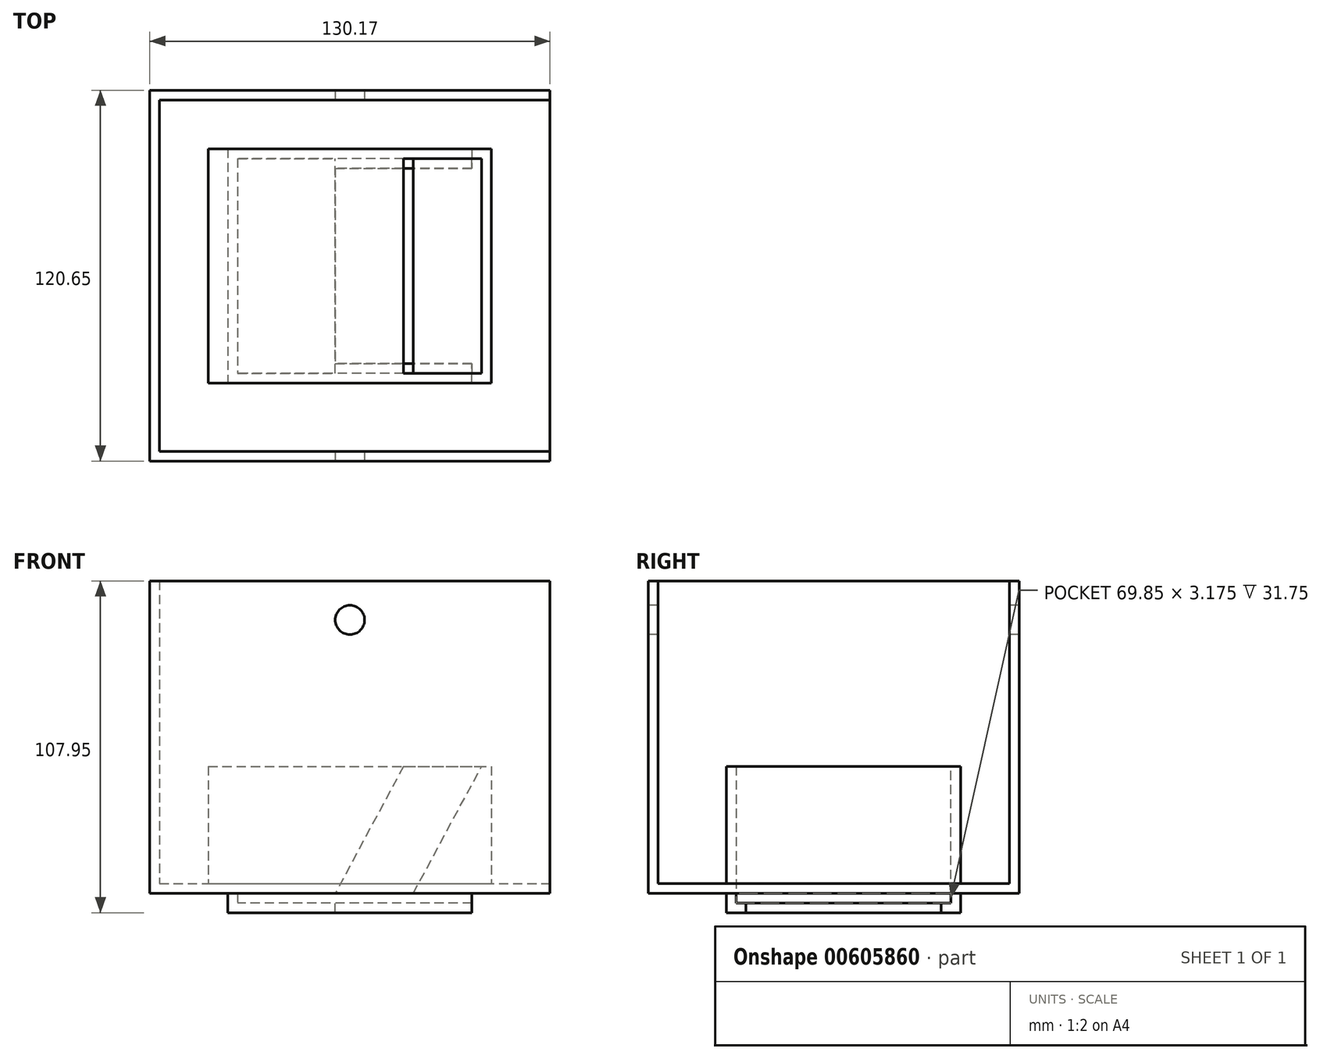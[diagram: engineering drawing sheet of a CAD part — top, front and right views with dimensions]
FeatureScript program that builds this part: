
annotation { "Feature Type Name" : "Feature", "Feature Type Description" : "" }
export const myFeature = defineFeature(function(context is Context, id is Id, definition is map)
    precondition{}
    {
        {
            var Q0;
            Q0=qCreatedBy(makeId("Top.planeOp"),FACE);
            var sketch = newSketch(context, id + "F0", { "sketchPlane" : qUnion([Q0])});
            skLineSegment(sketch, "E0.bottom", {"start": v(179.28, 0) * mm, "end": v(309.45, 0) * mm});
            skLineSegment(sketch, "E0.top", {"start": v(179.28, 120.65) * mm, "end": v(309.45, 120.65) * mm});
            skLineSegment(sketch, "E0.left", {"start": v(179.28, 0) * mm, "end": v(179.28, 120.65) * mm});
            skLineSegment(sketch, "E0.right", {"start": v(309.45, 0) * mm, "end": v(309.45, 120.65) * mm});
            skSolve(sketch);
        }
        {
            var Q0;
            Q0=makeQuery(id+"F0.imprint","IMPRINT",FACE,{"disambiguationData":[TD([[makeQuery(id+"F0.imprint","IMPRINT",EDGE,{"derivedFrom":sQuery(id+"F0.wireOp",EDGE,"E0.bottom")}),1.0]])]});
            extrude(context, id + "F1", {"entities" : qUnion([Q0]), "depth" : 101.6 * mm, "offsetDistance" : 25.4 * mm});
        }
        {
            var Q0;
            Q0=makeQuery(id+"F1.opExtrude","CAP_FACE",FACE,{"disambiguationData":[OSD([sQuery(id+"F0.wireOp",EDGE,"E0.bottom"),sQuery(id+"F0.wireOp",EDGE,"E0.top"),sQuery(id+"F0.wireOp",EDGE,"E0.left"),sQuery(id+"F0.wireOp",EDGE,"E0.right")])],"isStart":false});
            shell(context, id + "F2", {"entities" : qUnion([Q0]), "thickness" : 3.17 * mm});
        }
        {
            var Q0;
            Q0=makeQuery(id+"F2.opShell","OFFSET_FACE",FACE,{"disambiguationData":[OSD([sQuery(id+"F0.wireOp",EDGE,"E0.bottom"),sQuery(id+"F0.wireOp",EDGE,"E0.top"),sQuery(id+"F0.wireOp",EDGE,"E0.left"),sQuery(id+"F0.wireOp",EDGE,"E0.right")])]});
            var sketch = newSketch(context, id + "F3", { "sketchPlane" : qUnion([Q0])});
            skLineSegment(sketch, "E1.bottom", {"start": v(201.5, 98.43) * mm, "end": v(287.23, 98.43) * mm});
            skLineSegment(sketch, "E1.top", {"start": v(201.5, 28.58) * mm, "end": v(287.23, 28.58) * mm});
            skLineSegment(sketch, "E1.left", {"start": v(201.5, 98.43) * mm, "end": v(201.5, 28.58) * mm});
            skLineSegment(sketch, "E1.right", {"start": v(287.23, 98.43) * mm, "end": v(287.23, 28.58) * mm});
            skSolve(sketch);
        }
        {
            var Q0;
            Q0=makeQuery(id+"F3.imprint","IMPRINT",FACE,{"disambiguationData":[TD([[makeQuery(id+"F3.imprint","IMPRINT",EDGE,{"derivedFrom":sQuery(id+"F3.wireOp",EDGE,"E1.bottom")}),-1.0]])]});
            extrude(context, id + "F4", {"entities" : qUnion([Q0]), "operationType" : NewBodyOperationType.REMOVE, "oppositeDirection" : true, "depth" : 25.4 * mm, "offsetDistance" : 25.4 * mm});
        }
        {
            var Q0;
            Q0=makeQuery(id+"F2.opShell","OFFSET_FACE",FACE,{"disambiguationData":[OSD([sQuery(id+"F0.wireOp",EDGE,"E0.bottom"),sQuery(id+"F0.wireOp",EDGE,"E0.top"),sQuery(id+"F0.wireOp",EDGE,"E0.left"),sQuery(id+"F0.wireOp",EDGE,"E0.right")])]});
            var sketch = newSketch(context, id + "F5", { "sketchPlane" : qUnion([Q0])});
            skLineSegment(sketch, "E2.top", {"start": v(198.33, 25.4) * mm, "end": v(290.4, 25.4) * mm});
            skLineSegment(sketch, "E2.left", {"start": v(198.33, 101.6) * mm, "end": v(198.33, 25.4) * mm});
            skLineSegment(sketch, "E2.right", {"start": v(290.4, 101.6) * mm, "end": v(290.4, 25.4) * mm});
            skLineSegment(sketch, "E3", {"start": v(198.33, 101.6) * mm, "end": v(290.4, 101.6) * mm});
            skSolve(sketch);
        }
        {
            var Q0;
            Q0=makeQuery(id+"F5.imprint","IMPRINT",FACE,{"disambiguationData":[TD([[makeQuery(id+"F5.imprint","IMPRINT",EDGE,{"derivedFrom":sQuery(id+"F5.wireOp",EDGE,"E2.top")}),1.0]])]});
            extrude(context, id + "F6", {"entities" : qUnion([Q0]), "operationType" : NewBodyOperationType.ADD, "depth" : 38.1 * mm, "offsetDistance" : 25.4 * mm});
        }
        {
            var Q0;
            Q0=makeQuery(id+"F1.opExtrude","CAP_FACE",FACE,{"disambiguationData":[OSD([sQuery(id+"F0.wireOp",EDGE,"E0.bottom"),sQuery(id+"F0.wireOp",EDGE,"E0.top"),sQuery(id+"F0.wireOp",EDGE,"E0.left"),sQuery(id+"F0.wireOp",EDGE,"E0.right")])],"isStart":true});
            var sketch = newSketch(context, id + "F7", { "sketchPlane" : qUnion([Q0])});
            skLineSegment(sketch, "E4", {"start": v(204.68, -28.58) * mm, "end": v(204.68, -25.4) * mm});
            skLineSegment(sketch, "E5", {"start": v(204.68, -25.4) * mm, "end": v(284.05, -25.4) * mm});
            skLineSegment(sketch, "E6", {"start": v(284.05, -25.4) * mm, "end": v(284.05, -28.58) * mm});
            skSolve(sketch);
        }
        {
            var Q0;
            Q0 = qSketchRegion(id + "F7", true);
            var Q1;
            {var subQ0=sQuery(id+"F7.wireOp",EDGE,"E4");Q1=makeQuery(id+"F7.imprint","IMPRINT",FACE,{"disambiguationData":[TD([[makeQuery(id+"F7.imprint","IMPRINT",EDGE,{"derivedFrom":subQ0}),-1.0]])]});}
            extrude(context, id + "F8", {"entities" : qUnion([Q0, Q1]), "operationType" : NewBodyOperationType.ADD, "depth" : 6.35 * mm, "offsetDistance" : 25.4 * mm});
        }
        {
            var Q0;
            Q0=makeQuery(id+"F1.opExtrude","CAP_FACE",FACE,{"disambiguationData":[OSD([sQuery(id+"F0.wireOp",EDGE,"E0.bottom"),sQuery(id+"F0.wireOp",EDGE,"E0.top"),sQuery(id+"F0.wireOp",EDGE,"E0.left"),sQuery(id+"F0.wireOp",EDGE,"E0.right")])],"isStart":true});
            var sketch = newSketch(context, id + "F9", { "sketchPlane" : qUnion([Q0])});
            skLineSegment(sketch, "E7", {"start": v(204.68, -98.43) * mm, "end": v(204.68, -101.6) * mm});
            skLineSegment(sketch, "E8", {"start": v(204.68, -101.6) * mm, "end": v(284.05, -101.6) * mm});
            skLineSegment(sketch, "E9", {"start": v(284.05, -101.6) * mm, "end": v(284.05, -98.43) * mm});
            skSolve(sketch);
        }
        {
            var Q0;
            {var subQ0=sQuery(id+"F9.wireOp",EDGE,"E7");Q0=makeQuery(id+"F9.imprint","IMPRINT",FACE,{"disambiguationData":[TD([[makeQuery(id+"F9.imprint","IMPRINT",EDGE,{"derivedFrom":subQ0}),1.0]])]});}
            extrude(context, id + "F10", {"entities" : qUnion([Q0]), "operationType" : NewBodyOperationType.ADD, "depth" : 6.35 * mm, "offsetDistance" : 25.4 * mm});
        }
        {
            var Q0;
            {var subQ0=sQuery(id+"F3.wireOp",EDGE,"E1.bottom");Q0=makeQuery(id+"F10.boolean.opBoolean","MERGE",FACE,{"derivedFrom":[makeQuery(id+"F6.boolean.opBoolean","MERGE",FACE,{"derivedFrom":[makeQuery(id+"F4.boolean.opBoolean","COPY",FACE,{"derivedFrom":makeQuery(id+"F4.opExtrude","SWEPT_FACE",FACE,{"disambiguationData":[OSD([subQ0])]})}),makeQuery(id+"F6.opExtrude","SWEPT_FACE",FACE,{"disambiguationData":[OSD([subQ0])]})]}),makeQuery(id+"F10.opExtrude","SWEPT_FACE",FACE,{"disambiguationData":[OSD([sQuery(id+"F0.wireOp",EDGE,"E0.bottom"),sQuery(id+"F0.wireOp",EDGE,"E0.top"),sQuery(id+"F0.wireOp",EDGE,"E0.left"),sQuery(id+"F0.wireOp",EDGE,"E0.right"),subQ0])]})]});}
            var sketch = newSketch(context, id + "F11", { "sketchPlane" : qUnion([Q0])});
            skLineSegment(sketch, "E10.bottom", {"start": v(284.05, -6.35) * mm, "end": v(204.68, -6.35) * mm});
            skLineSegment(sketch, "E10.top", {"start": v(284.05, -3.18) * mm, "end": v(204.68, -3.18) * mm});
            skLineSegment(sketch, "E10.left", {"start": v(284.05, -6.35) * mm, "end": v(284.05, -3.18) * mm});
            skLineSegment(sketch, "E10.right", {"start": v(204.68, -6.35) * mm, "end": v(204.68, -3.18) * mm});
            skSolve(sketch);
        }
        {
            var Q0;
            Q0=makeQuery(id+"F11.imprint","IMPRINT",FACE,{"disambiguationData":[TD([[makeQuery(id+"F11.imprint","IMPRINT",EDGE,{"derivedFrom":sQuery(id+"F11.wireOp",EDGE,"E10.bottom")}),1.0]])]});
            extrude(context, id + "F12", {"entities" : qUnion([Q0]), "operationType" : NewBodyOperationType.ADD, "depth" : 3.17 * mm, "offsetDistance" : 25.4 * mm});
        }
        {
            var Q0;
            {var subQ0=sQuery(id+"F3.wireOp",EDGE,"E1.top");Q0=makeQuery(id+"F8.boolean.opBoolean","MERGE",FACE,{"derivedFrom":[makeQuery(id+"F6.boolean.opBoolean","MERGE",FACE,{"derivedFrom":[makeQuery(id+"F4.boolean.opBoolean","COPY",FACE,{"derivedFrom":makeQuery(id+"F4.opExtrude","SWEPT_FACE",FACE,{"disambiguationData":[OSD([subQ0])]})}),makeQuery(id+"F6.opExtrude","SWEPT_FACE",FACE,{"disambiguationData":[OSD([subQ0])]})]}),makeQuery(id+"F8.opExtrude","SWEPT_FACE",FACE,{"disambiguationData":[OSD([sQuery(id+"F0.wireOp",EDGE,"E0.bottom"),sQuery(id+"F0.wireOp",EDGE,"E0.top"),sQuery(id+"F0.wireOp",EDGE,"E0.left"),sQuery(id+"F0.wireOp",EDGE,"E0.right"),subQ0])]})]});}
            var sketch = newSketch(context, id + "F13", { "sketchPlane" : qUnion([Q0])});
            skLineSegment(sketch, "E11.bottom", {"start": v(-284.05, -6.35) * mm, "end": v(-204.68, -6.35) * mm});
            skLineSegment(sketch, "E11.top", {"start": v(-284.05, -3.18) * mm, "end": v(-204.68, -3.18) * mm});
            skLineSegment(sketch, "E11.left", {"start": v(-284.05, -6.35) * mm, "end": v(-284.05, -3.18) * mm});
            skLineSegment(sketch, "E11.right", {"start": v(-204.68, -6.35) * mm, "end": v(-204.68, -3.18) * mm});
            skSolve(sketch);
        }
        {
            var Q0;
            Q0=makeQuery(id+"F13.imprint","IMPRINT",FACE,{"disambiguationData":[TD([[makeQuery(id+"F13.imprint","IMPRINT",EDGE,{"derivedFrom":sQuery(id+"F13.wireOp",EDGE,"E11.bottom")}),-1.0]])]});
            extrude(context, id + "F14", {"entities" : qUnion([Q0]), "operationType" : NewBodyOperationType.ADD, "depth" : 3.17 * mm, "offsetDistance" : 25.4 * mm});
        }
        {
            var Q0;
            Q0=makeQuery(id+"F1.opExtrude","SWEPT_FACE",FACE,{"disambiguationData":[OSD([sQuery(id+"F0.wireOp",EDGE,"E0.right")])]});
            var sketch = newSketch(context, id + "F15", { "sketchPlane" : qUnion([Q0])});
            skLineSegment(sketch, "E12.bottom", {"start": v(3.17, 98.43) * mm, "end": v(117.47, 98.43) * mm});
            skLineSegment(sketch, "E12.top", {"start": v(3.17, 3.18) * mm, "end": v(117.47, 3.18) * mm});
            skLineSegment(sketch, "E12.left", {"start": v(3.17, 98.43) * mm, "end": v(3.17, 3.17) * mm});
            skLineSegment(sketch, "E12.right", {"start": v(117.47, 98.43) * mm, "end": v(117.47, 3.17) * mm});
            skSolve(sketch);
        }
        {
            var Q0;
            Q0=makeQuery(id+"F15.imprint","IMPRINT",FACE,{"disambiguationData":[TD([[makeQuery(id+"F15.imprint","IMPRINT",EDGE,{"derivedFrom":sQuery(id+"F15.wireOp",EDGE,"E12.bottom")}),-1.0]])]});
            extrude(context, id + "F16", {"entities" : qUnion([Q0]), "operationType" : NewBodyOperationType.REMOVE, "oppositeDirection" : true, "depth" : 6.35 * mm, "offsetDistance" : 25.4 * mm});
        }
        {
            var Q0;
            Q0=makeQuery(id+"F1.opExtrude","SWEPT_FACE",FACE,{"disambiguationData":[OSD([sQuery(id+"F0.wireOp",EDGE,"E0.right")])]});
            var sketch = newSketch(context, id + "F17", { "sketchPlane" : qUnion([Q0])});
            skLineSegment(sketch, "E13", {"start": v(3.17, 98.43) * mm, "end": v(3.17, 101.6) * mm});
            skLineSegment(sketch, "E14", {"start": v(117.47, 98.43) * mm, "end": v(117.47, 101.6) * mm});
            skSolve(sketch);
        }
        {
            var Q0;
            Q0 = qSketchRegion(id + "F17", true);
            var Q1;
            {var subQ0=sQuery(id+"F17.wireOp",EDGE,"E13");Q1=makeQuery(id+"F17.imprint","IMPRINT",FACE,{"disambiguationData":[TD([[makeQuery(id+"F17.imprint","IMPRINT",EDGE,{"derivedFrom":subQ0}),-1.0]])]});}
            extrude(context, id + "F18", {"entities" : qUnion([Q0, Q1]), "operationType" : NewBodyOperationType.REMOVE, "oppositeDirection" : true, "depth" : 16.76 * mm, "offsetDistance" : 25.4 * mm});
        }
        {
            var Q0;
            {var subQ0=sQuery(id+"F3.wireOp",EDGE,"E1.bottom");Q0=makeQuery(id+"F10.boolean.opBoolean","MERGE",FACE,{"derivedFrom":[makeQuery(id+"F6.boolean.opBoolean","MERGE",FACE,{"derivedFrom":[makeQuery(id+"F4.boolean.opBoolean","COPY",FACE,{"derivedFrom":makeQuery(id+"F4.opExtrude","SWEPT_FACE",FACE,{"disambiguationData":[OSD([subQ0])]})}),makeQuery(id+"F6.opExtrude","SWEPT_FACE",FACE,{"disambiguationData":[OSD([subQ0])]})]}),makeQuery(id+"F10.opExtrude","SWEPT_FACE",FACE,{"disambiguationData":[OSD([sQuery(id+"F0.wireOp",EDGE,"E0.bottom"),sQuery(id+"F0.wireOp",EDGE,"E0.top"),sQuery(id+"F0.wireOp",EDGE,"E0.left"),sQuery(id+"F0.wireOp",EDGE,"E0.right"),subQ0])]})]});}
            var sketch = newSketch(context, id + "F19", { "sketchPlane" : qUnion([Q0])});
            skLineSegment(sketch, "E15", {"start": v(284.05, 0) * mm, "end": v(265, 0) * mm});
            skPoint(sketch, "E15.endSnap0", {"position": v(285.64, 0) * mm});
            skLineSegment(sketch, "E16", {"start": v(265, 0) * mm, "end": v(287.23, 41.27) * mm});
            skSolve(sketch);
        }
        {
            var Q0;
            Q0 = qSketchRegion(id + "F19", true);
            var Q1;
            Q1=makeQuery(id+"F19.imprint","IMPRINT",FACE,{"disambiguationData":[TD([[makeQuery(id+"F19.imprint","IMPRINT",EDGE,{"derivedFrom":sQuery(id+"F19.wireOp",EDGE,"E15")}),-1.0]])]});
            extrude(context, id + "F20", {"entities" : qUnion([Q0, Q1]), "operationType" : NewBodyOperationType.ADD, "depth" : 69.85 * mm, "offsetDistance" : 25.4 * mm});
        }
        {
            var Q0;
            {var subQ0=sQuery(id+"F3.wireOp",EDGE,"E1.bottom");Q0=makeQuery(id+"F10.boolean.opBoolean","MERGE",FACE,{"derivedFrom":[makeQuery(id+"F6.boolean.opBoolean","MERGE",FACE,{"derivedFrom":[makeQuery(id+"F4.boolean.opBoolean","COPY",FACE,{"derivedFrom":makeQuery(id+"F4.opExtrude","SWEPT_FACE",FACE,{"disambiguationData":[OSD([subQ0])]})}),makeQuery(id+"F6.opExtrude","SWEPT_FACE",FACE,{"disambiguationData":[OSD([subQ0])]})]}),makeQuery(id+"F10.opExtrude","SWEPT_FACE",FACE,{"disambiguationData":[OSD([sQuery(id+"F0.wireOp",EDGE,"E0.bottom"),sQuery(id+"F0.wireOp",EDGE,"E0.top"),sQuery(id+"F0.wireOp",EDGE,"E0.left"),sQuery(id+"F0.wireOp",EDGE,"E0.right"),subQ0])]})]});}
            var sketch = newSketch(context, id + "F21", { "sketchPlane" : qUnion([Q0])});
            skLineSegment(sketch, "E17", {"start": v(204.68, 0) * mm, "end": v(239.6, 0) * mm});
            skLineSegment(sketch, "E18", {"start": v(261.83, 41.27) * mm, "end": v(239.6, 0) * mm});
            skSolve(sketch);
        }
        {
            var Q0;
            Q0 = qSketchRegion(id + "F21", true);
            var Q1;
            Q1=makeQuery(id+"F21.imprint","IMPRINT",FACE,{"disambiguationData":[TD([[makeQuery(id+"F21.imprint","IMPRINT",EDGE,{"derivedFrom":sQuery(id+"F21.wireOp",EDGE,"E17")}),1.0]])]});
            extrude(context, id + "F22", {"entities" : qUnion([Q0, Q1]), "operationType" : NewBodyOperationType.ADD, "depth" : 69.85 * mm, "offsetDistance" : 25.4 * mm});
        }
        {
            var Q0;
            Q0=makeQuery(id+"F1.opExtrude","SWEPT_FACE",FACE,{"disambiguationData":[OSD([sQuery(id+"F0.wireOp",EDGE,"E0.bottom")])]});
            var sketch = newSketch(context, id + "F23", { "sketchPlane" : qUnion([Q0])});
            skLineSegment(sketch, "E19", {"start": v(179.28, 101.6) * mm, "end": v(309.45, 101.6) * mm});
            skPoint(sketch, "E20.endSnap0", {"position": v(244.36, 101.6) * mm});
            skCircle(sketch, "E21", {"center": v(244.36, 88.9) * mm, "radius": 4.76 * mm});
            skSolve(sketch);
        }
        {
            var Q0;
            Q0=makeQuery(id+"F23.imprint","IMPRINT",FACE,{"disambiguationData":[TD([[makeQuery(id+"F23.imprint","IMPRINT",EDGE,{"derivedFrom":sQuery(id+"F23.wireOp",EDGE,"E21")}),1.0]])]});
            extrude(context, id + "F24", {"entities" : qUnion([Q0]), "operationType" : NewBodyOperationType.REMOVE, "oppositeDirection" : true, "depth" : 148.08 * mm, "offsetDistance" : 25.4 * mm});
        }
        {
            var Q0;
            {var subQ0=sQuery(id+"F3.wireOp",EDGE,"E1.top");Q0=makeQuery(id+"F8.boolean.opBoolean","MERGE",FACE,{"derivedFrom":[makeQuery(id+"F6.boolean.opBoolean","MERGE",FACE,{"derivedFrom":[makeQuery(id+"F4.boolean.opBoolean","COPY",FACE,{"derivedFrom":makeQuery(id+"F4.opExtrude","SWEPT_FACE",FACE,{"disambiguationData":[OSD([subQ0])]})}),makeQuery(id+"F6.opExtrude","SWEPT_FACE",FACE,{"disambiguationData":[OSD([subQ0])]})]}),makeQuery(id+"F8.opExtrude","SWEPT_FACE",FACE,{"disambiguationData":[OSD([sQuery(id+"F0.wireOp",EDGE,"E0.bottom"),sQuery(id+"F0.wireOp",EDGE,"E0.top"),sQuery(id+"F0.wireOp",EDGE,"E0.left"),sQuery(id+"F0.wireOp",EDGE,"E0.right"),subQ0])]})]});}
            var sketch = newSketch(context, id + "F25", { "sketchPlane" : qUnion([Q0])});
            skLineSegment(sketch, "E22", {"start": v(-204.68, 0) * mm, "end": v(-207.85, 0) * mm});
            skLineSegment(sketch, "E23", {"start": v(-207.85, 0) * mm, "end": v(-207.85, -3.18) * mm});
            skSolve(sketch);
        }
        {
            var Q0;
            Q0=makeQuery(id+"F25.imprint","IMPRINT",FACE,{"disambiguationData":[TD([[makeQuery(id+"F25.imprint","IMPRINT",EDGE,{"derivedFrom":sQuery(id+"F25.wireOp",EDGE,"E22")}),1.0]])]});
            extrude(context, id + "F26", {"entities" : qUnion([Q0]), "operationType" : NewBodyOperationType.ADD, "depth" : 69.85 * mm, "offsetDistance" : 25.4 * mm});
        }
        {
            var Q0;
            Q0=makeQuery(id+"F26.opExtrude","SWEPT_FACE",FACE,{"disambiguationData":[OSD([sQuery(id+"F13.wireOp",EDGE,"E11.top")])]});
            extrude(context, id + "F27", {"entities" : qUnion([Q0]), "operationType" : NewBodyOperationType.ADD, "depth" : 3.17 * mm, "offsetDistance" : 25.4 * mm});
        }
        {
            var Q0;
            {var subQ0=sQuery(id+"F25.wireOp",EDGE,"E23");Q0=makeQuery(id+"F27.boolean.opBoolean","MERGE",FACE,{"derivedFrom":[makeQuery(id+"F26.opExtrude","SWEPT_FACE",FACE,{"disambiguationData":[OSD([subQ0])]}),makeQuery(id+"F27.opExtrude","SWEPT_FACE",FACE,{"disambiguationData":[OSD([sQuery(id+"F13.wireOp",EDGE,"E11.top"),subQ0])]})]});}
            var sketch = newSketch(context, id + "F28", { "sketchPlane" : qUnion([Q0])});
            skLineSegment(sketch, "E24", {"start": v(95.25, -3.18) * mm, "end": v(31.75, -3.18) * mm});
            skSolve(sketch);
        }
        {
            var Q0;
            Q0=makeQuery(id+"F28.imprint","IMPRINT",FACE,{"disambiguationData":[TD([[makeQuery(id+"F28.imprint","IMPRINT",EDGE,{"derivedFrom":sQuery(id+"F28.wireOp",EDGE,"E24")}),1.0]])]});
            extrude(context, id + "F29", {"entities" : qUnion([Q0]), "operationType" : NewBodyOperationType.ADD, "depth" : 31.75 * mm, "offsetDistance" : 25.4 * mm});
        }
    });
